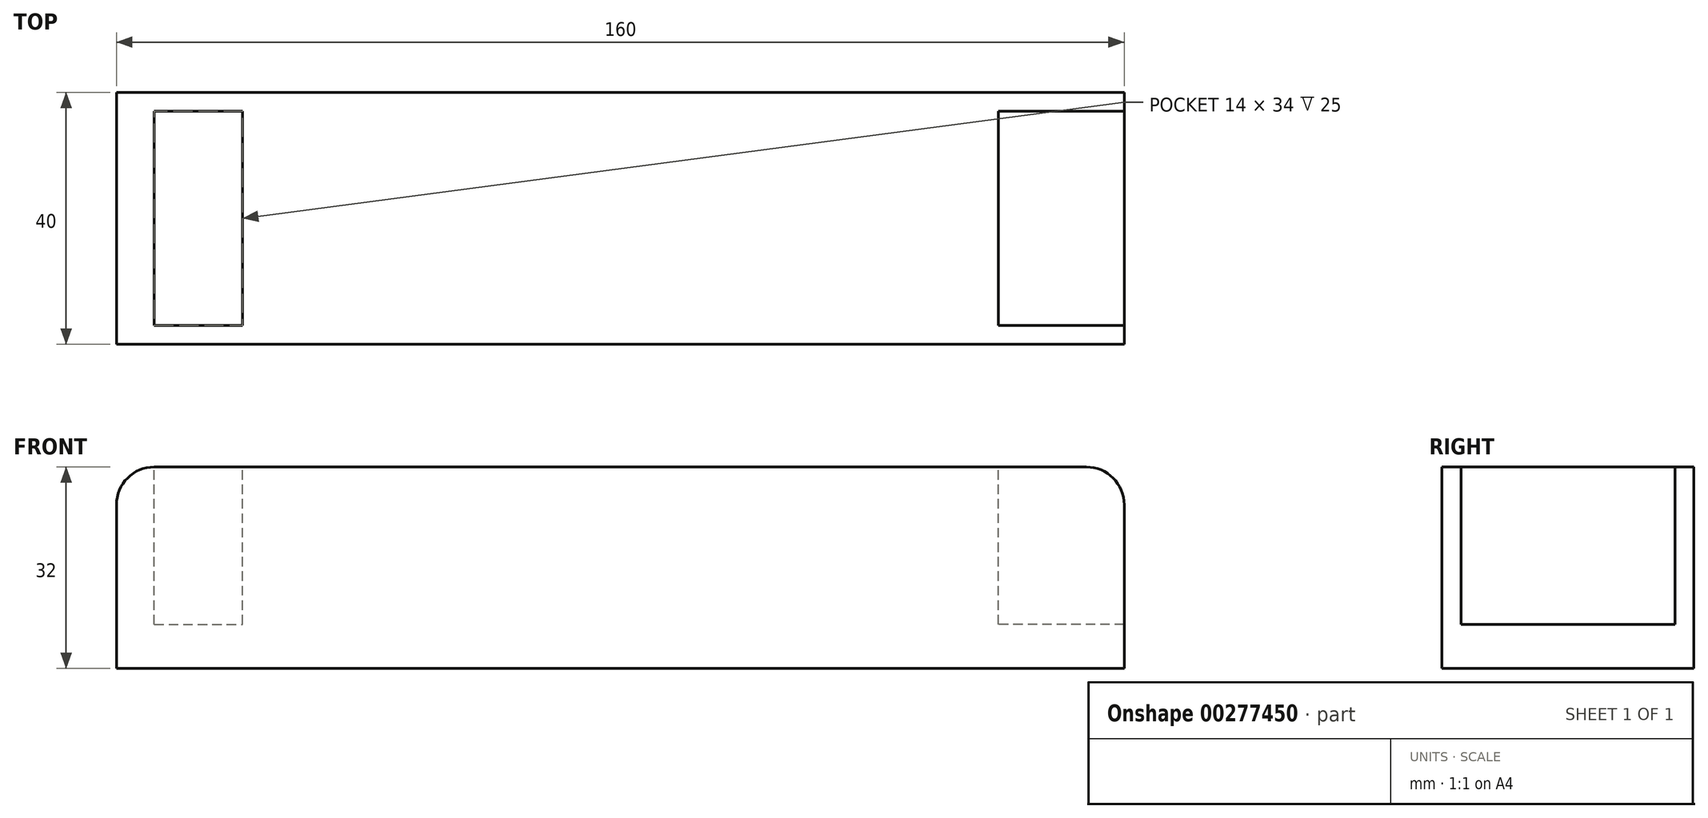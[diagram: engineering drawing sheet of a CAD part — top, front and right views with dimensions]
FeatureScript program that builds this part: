
annotation { "Feature Type Name" : "Feature", "Feature Type Description" : "" }
export const myFeature = defineFeature(function(context is Context, id is Id, definition is map)
    precondition{}
    {
        {
            var Q0;
            Q0=qCreatedBy(makeId("Top.planeOp"),FACE);
            var sketch = newSketch(context, id + "F0", { "sketchPlane" : qUnion([Q0])});
            skLineSegment(sketch, "E0.bottom", {"start": v(80, 20) * mm, "end": v(-80, 20) * mm});
            skLineSegment(sketch, "E0.top", {"start": v(80, -20) * mm, "end": v(-80, -20) * mm});
            skLineSegment(sketch, "E0.left", {"start": v(80, 20) * mm, "end": v(80, -20) * mm});
            skLineSegment(sketch, "E0.right", {"start": v(-80, 20) * mm, "end": v(-80, -20) * mm});
            skPoint(sketch, "E0.middle", {"position": v(0, 0) * mm});
            skSolve(sketch);
        }
        {
            var Q0;
            Q0 = qSketchRegion(id + "F0", true);
            extrude(context, id + "F1", {"entities" : qUnion([Q0]), "depth" : 32 * mm});
        }
        {
            var Q0;
            Q0=makeQuery(id+"F1.opExtrude","SWEPT_FACE",FACE,{"disambiguationData":[OSD([sQuery(id+"F0.wireOp",EDGE,"E0.top")])]});
            var sketch = newSketch(context, id + "F2", { "sketchPlane" : qUnion([Q0])});
            skLineSegment(sketch, "E1.0", {"start": v(74, 32) * mm, "end": v(-74, 32) * mm});
            skLineSegment(sketch, "E2.0", {"start": v(-80, 26) * mm, "end": v(-80, 0) * mm});
            skPoint(sketch, "E3.0", {"position": v(80, 16) * mm});
            skLineSegment(sketch, "E4.0", {"start": v(80, 26) * mm, "end": v(80, 0) * mm});
            skPoint(sketch, "E5.visualSharp", {"position": v(-80, 32) * mm});
            skArc(sketch, "E5.filletArc", {"start": v(-74, 32) * mm, "mid": v(-78.24, 30.24) * mm, "end": v(-80, 26) * mm});
            skPoint(sketch, "E6.visualSharp", {"position": v(80, 32) * mm});
            skArc(sketch, "E6.filletArc", {"start": v(80, 26) * mm, "mid": v(78.24, 30.24) * mm, "end": v(74, 32) * mm});
            skSolve(sketch);
        }
        {
            var Q0;
            {var subQ0=sQuery(id+"F2.wireOp",EDGE,"E5.filletArc");Q0=makeQuery(id+"F2.imprint","IMPRINT",FACE,{"disambiguationData":[TD([[makeQuery(id+"F2.imprint","IMPRINT",EDGE,{"derivedFrom":subQ0}),-1.0]])]});}
            var Q1;
            {var subQ0=sQuery(id+"F2.wireOp",EDGE,"E6.filletArc");Q1=makeQuery(id+"F2.imprint","IMPRINT",FACE,{"disambiguationData":[TD([[makeQuery(id+"F2.imprint","IMPRINT",EDGE,{"derivedFrom":subQ0}),-1.0]])]});}
            extrude(context, id + "F3", {"entities" : qUnion([Q0, Q1]), "operationType" : NewBodyOperationType.REMOVE, "endBound" : BoundingType.THROUGH_ALL, "oppositeDirection" : true, "depth" : 25 * mm});
        }
        {
            var Q0;
            Q0=makeQuery(id+"F1.opExtrude","CAP_FACE",FACE,{"disambiguationData":[OSD([sQuery(id+"F0.wireOp",EDGE,"E0.bottom"),sQuery(id+"F0.wireOp",EDGE,"E0.top"),sQuery(id+"F0.wireOp",EDGE,"E0.left"),sQuery(id+"F0.wireOp",EDGE,"E0.right")])],"isStart":false});
            var sketch = newSketch(context, id + "F4", { "sketchPlane" : qUnion([Q0])});
            skLineSegment(sketch, "E7.0", {"start": v(-80, 20) * mm, "end": v(-80, -20) * mm});
            skLineSegment(sketch, "E8.0", {"start": v(-74, 20) * mm, "end": v(-74, -20) * mm});
            skLineSegment(sketch, "E9.0", {"start": v(80, 20) * mm, "end": v(80, -20) * mm});
            skLineSegment(sketch, "E10.0", {"start": v(74, 20) * mm, "end": v(74, -20) * mm});
            skLineSegment(sketch, "E11.bottom", {"start": v(-80, 17) * mm, "end": v(-60, 17) * mm});
            skLineSegment(sketch, "E11.top", {"start": v(-80, -17) * mm, "end": v(-60, -17) * mm});
            skLineSegment(sketch, "E11.left", {"start": v(-80, 17) * mm, "end": v(-80, -17) * mm});
            skLineSegment(sketch, "E11.right", {"start": v(-60, 17) * mm, "end": v(-60, -17) * mm});
            skLineSegment(sketch, "E12", {"start": v(0, 20) * mm, "end": v(0, -20) * mm, "construction": true});
            skLineSegment(sketch, "E13.MirrorCS", {"start": v(80, 17) * mm, "end": v(60, 17) * mm});
            skLineSegment(sketch, "E14.MirrorCS", {"start": v(60, 17) * mm, "end": v(60, -17) * mm});
            skLineSegment(sketch, "E15.MirrorCS", {"start": v(80, -17) * mm, "end": v(60, -17) * mm});
            skSolve(sketch);
        }
        {
            var Q0;
            {var subQ0=sQuery(id+"F4.wireOp",EDGE,"E13.MirrorCS");var subQ1=sQuery(id+"F4.wireOp",EDGE,"E9.0");var subQ2=makeQuery(id+"F4.imprint","INTERSECT",VERTEX,{"derivedFrom":[subQ1,subQ0]});Q0=makeQuery(id+"F4.imprint","IMPRINT",FACE,{"disambiguationData":[TD([[makeQuery(id+"F4.imprint","IMPRINT",EDGE,{"disambiguationData":[TD([[subQ2,-1.0]])],"derivedFrom":subQ1}),-1.0]])]});}
            var Q1;
            {var subQ5=sQuery(id+"F4.wireOp",EDGE,"E11.right");Q1=makeQuery(id+"F4.imprint","IMPRINT",FACE,{"disambiguationData":[TD([[makeQuery(id+"F4.imprint","IMPRINT",EDGE,{"derivedFrom":subQ5}),-1.0]])]});}
            var Q2;
            {var subQ5=sQuery(id+"F4.wireOp",EDGE,"E14.MirrorCS");Q2=makeQuery(id+"F4.imprint","IMPRINT",FACE,{"disambiguationData":[TD([[makeQuery(id+"F4.imprint","IMPRINT",EDGE,{"derivedFrom":subQ5}),1.0]])]});}
            var Q3;
            {var subQ5=sQuery(id+"F4.wireOp",EDGE,"E11.left");Q3=makeQuery(id+"F4.imprint","IMPRINT",FACE,{"disambiguationData":[TD([[makeQuery(id+"F4.imprint","IMPRINT",EDGE,{"derivedFrom":subQ5}),1.0]])]});}
            extrude(context, id + "F5", {"entities" : qUnion([Q0, Q1, Q2, Q3]), "operationType" : NewBodyOperationType.REMOVE, "oppositeDirection" : true, "depth" : 25 * mm});
        }
    });
